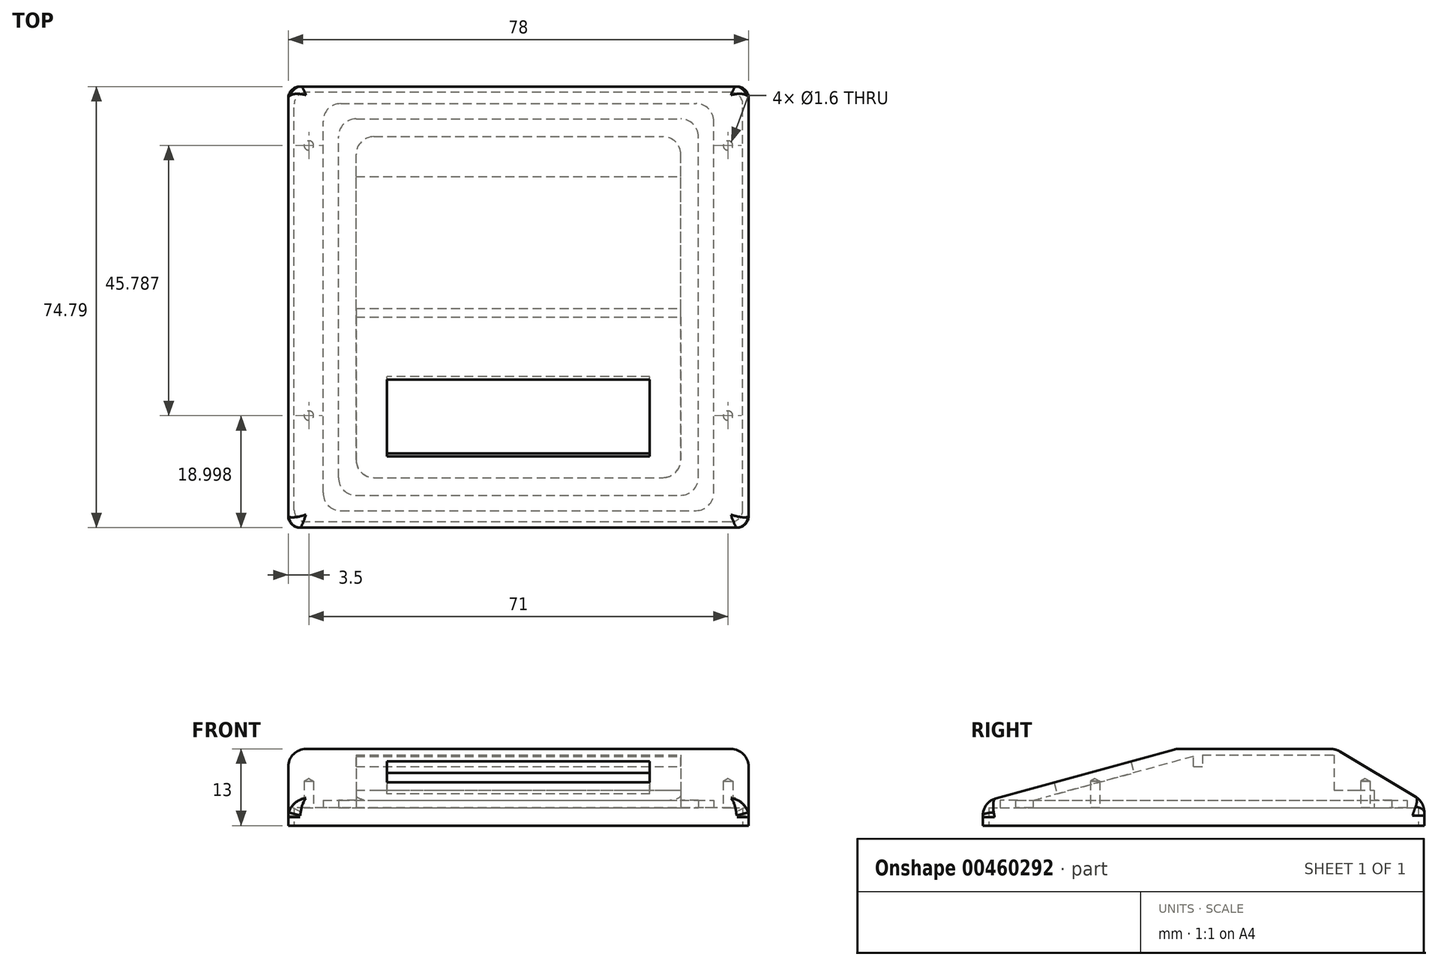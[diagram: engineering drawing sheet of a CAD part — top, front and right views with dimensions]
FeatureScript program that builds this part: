
annotation { "Feature Type Name" : "Feature", "Feature Type Description" : "" }
export const myFeature = defineFeature(function(context is Context, id is Id, definition is map)
    precondition{}
    {
        {
            var Q0;
            Q0=qCreatedBy(makeId("Right.planeOp"),FACE);
            var sketch = newSketch(context, id + "F0", { "sketchPlane" : qUnion([Q0])});
            skLineSegment(sketch, "E0", {"start": v(13.67, 15.98) * mm, "end": v(40.67, 15.98) * mm});
            skLineSegment(sketch, "E1", {"start": v(40.67, 15.98) * mm, "end": v(55.67, 6.98) * mm});
            skLineSegment(sketch, "E2", {"start": v(13.67, 15.98) * mm, "end": v(-19.12, 6.98) * mm});
            skLineSegment(sketch, "E3", {"start": v(-19.12, 6.98) * mm, "end": v(-19.12, 2.98) * mm});
            skLineSegment(sketch, "E4", {"start": v(-19.12, 2.98) * mm, "end": v(55.67, 2.98) * mm});
            skLineSegment(sketch, "E5", {"start": v(55.67, 6.98) * mm, "end": v(55.67, 2.98) * mm});
            skSolve(sketch);
        }
        {
            var Q0;
            Q0 = qSketchRegion(id + "F0", true);
            extrude(context, id + "F1", {"entities" : qUnion([Q0]), "depth" : 78 * mm, "offsetDistance" : 25 * mm});
        }
        {
            var Q0;
            Q0=makeQuery(id+"F1.opExtrude","CAP_FACE",FACE,{"disambiguationData":[OSD([sQuery(id+"F0.wireOp",EDGE,"E0"),sQuery(id+"F0.wireOp",EDGE,"E1"),sQuery(id+"F0.wireOp",EDGE,"E2"),sQuery(id+"F0.wireOp",EDGE,"E3"),sQuery(id+"F0.wireOp",EDGE,"E4"),sQuery(id+"F0.wireOp",EDGE,"E5")])],"isStart":false});
            cPlane(context, id + "F2", {"entities" : qUnion([Q0]), "cplaneType" : CPlaneType.OFFSET, "offset" : 11.5 * mm, "oppositeDirection" : true, "width" : 150 * mm, "height" : 150 * mm});
        }
        {
            var Q0;
            Q0=qCreatedBy(id+"F2.planeOp",FACE);
            var sketch = newSketch(context, id + "F3", { "sketchPlane" : qUnion([Q0])});
            skLineSegment(sketch, "E6.0", {"start": v(40.39, 14.98) * mm, "end": v(47.17, 10.92) * mm});
            skLineSegment(sketch, "E7.0", {"start": v(17.58, 14.98) * mm, "end": v(-10.62, 7.24) * mm});
            skLineSegment(sketch, "E8.0", {"start": v(-10.62, 2.98) * mm, "end": v(47.17, 2.98) * mm});
            skLineSegment(sketch, "E9", {"start": v(-10.62, 7.24) * mm, "end": v(-10.62, 2.98) * mm});
            skLineSegment(sketch, "E10", {"start": v(17.58, 14.98) * mm, "end": v(40.39, 14.98) * mm});
            skLineSegment(sketch, "E11", {"start": v(47.17, 10.92) * mm, "end": v(47.17, 2.98) * mm});
            skSolve(sketch);
        }
        {
            var Q0;
            Q0 = qSketchRegion(id + "F3", true);
            extrude(context, id + "F4", {"entities" : qUnion([Q0]), "operationType" : NewBodyOperationType.REMOVE, "oppositeDirection" : true, "depth" : 55 * mm, "offsetDistance" : 25 * mm});
        }
        {
            var Q0;
            Q0=makeQuery(id+"F4.boolean.opBoolean","COPY",FACE,{"derivedFrom":makeQuery(id+"F4.opExtrude","SWEPT_FACE",FACE,{"disambiguationData":[OSD([sQuery(id+"F3.wireOp",EDGE,"E7.0")])]})});
            var sketch = newSketch(context, id + "F5", { "sketchPlane" : qUnion([Q0])});
            skLineSegment(sketch, "E12.bottom", {"start": v(61.25, 4.08) * mm, "end": v(16.75, 4.08) * mm});
            skLineSegment(sketch, "E12.top", {"start": v(61.25, -9.42) * mm, "end": v(16.75, -9.42) * mm});
            skLineSegment(sketch, "E12.left", {"start": v(61.25, 4.08) * mm, "end": v(61.25, -9.42) * mm});
            skLineSegment(sketch, "E12.right", {"start": v(16.75, 4.08) * mm, "end": v(16.75, -9.42) * mm});
            skSolve(sketch);
        }
        {
            var Q0;
            Q0 = qSketchRegion(id + "F5", true);
            extrude(context, id + "F6", {"entities" : qUnion([Q0]), "operationType" : NewBodyOperationType.REMOVE, "endBound" : BoundingType.UP_TO_NEXT, "oppositeDirection" : true, "depth" : 25 * mm});
        }
        {
            var Q0;
            Q0=makeQuery(id+"F1.opExtrude","SWEPT_FACE",FACE,{"disambiguationData":[OSD([sQuery(id+"F0.wireOp",EDGE,"E4")])]});
            var sketch = newSketch(context, id + "F7", { "sketchPlane" : qUnion([Q0])});
            skLineSegment(sketch, "E13.0", {"start": v(77, 18.12) * mm, "end": v(77, -54.67) * mm});
            skLineSegment(sketch, "E13.1", {"start": v(77, 18.12) * mm, "end": v(1, 18.12) * mm});
            skLineSegment(sketch, "E13.2", {"start": v(1, 18.12) * mm, "end": v(1, -54.67) * mm});
            skLineSegment(sketch, "E13.3", {"start": v(77, -54.67) * mm, "end": v(1, -54.67) * mm});
            skLineSegment(sketch, "E14.0", {"start": v(66.5, 10.62) * mm, "end": v(66.5, -47.17) * mm});
            skLineSegment(sketch, "E14.1", {"start": v(11.5, 10.62) * mm, "end": v(66.5, 10.62) * mm});
            skLineSegment(sketch, "E14.2", {"start": v(11.5, 10.62) * mm, "end": v(11.5, -47.17) * mm});
            skLineSegment(sketch, "E14.3", {"start": v(11.5, -47.17) * mm, "end": v(66.5, -47.17) * mm});
            skPoint(sketch, "E15.visualSharp", {"position": v(77, 18.12) * mm});
            skPoint(sketch, "E16.visualSharp", {"position": v(1, 18.12) * mm});
            skPoint(sketch, "E17.visualSharp", {"position": v(77, -54.67) * mm});
            skPoint(sketch, "E18.visualSharp", {"position": v(1, -54.67) * mm});
            skSolve(sketch);
        }
        {
            var Q0;
            Q0 = qSketchRegion(id + "F7", true);
            extrude(context, id + "F8", {"entities" : qUnion([Q0]), "operationType" : NewBodyOperationType.REMOVE, "oppositeDirection" : true, "depth" : 3 * mm});
        }
        {
            var Q0;
            Q0=makeQuery(id+"F8.boolean.opBoolean","COPY",FACE,{"derivedFrom":makeQuery(id+"F8.opExtrude","CAP_FACE",FACE,{"disambiguationData":[OSD([sQuery(id+"F7.wireOp",EDGE,"E13.0"),sQuery(id+"F7.wireOp",EDGE,"E13.1"),sQuery(id+"F7.wireOp",EDGE,"E13.2"),sQuery(id+"F7.wireOp",EDGE,"E13.3"),sQuery(id+"F7.wireOp",EDGE,"E14.0"),sQuery(id+"F7.wireOp",EDGE,"E14.1"),sQuery(id+"F7.wireOp",EDGE,"E14.2"),sQuery(id+"F7.wireOp",EDGE,"E14.3"),sQuery(id+"F7.wireOp",EDGE,"E15.filletArc"),sQuery(id+"F7.wireOp",EDGE,"E16.filletArc"),sQuery(id+"F7.wireOp",EDGE,"E17.filletArc"),sQuery(id+"F7.wireOp",EDGE,"E18.filletArc")])],"isStart":false})});
            var sketch = newSketch(context, id + "F9", { "sketchPlane" : qUnion([Q0])});
            skLineSegment(sketch, "E19.0", {"start": v(69.5, 13.62) * mm, "end": v(69.5, -50.17) * mm});
            skLineSegment(sketch, "E19.1", {"start": v(8.5, 13.62) * mm, "end": v(69.5, 13.62) * mm});
            skLineSegment(sketch, "E19.2", {"start": v(8.5, 13.62) * mm, "end": v(8.5, -50.17) * mm});
            skLineSegment(sketch, "E19.3", {"start": v(8.5, -50.17) * mm, "end": v(69.5, -50.17) * mm});
            skLineSegment(sketch, "E20.0", {"start": v(72.1, 16.22) * mm, "end": v(72.1, -52.77) * mm});
            skLineSegment(sketch, "E20.1", {"start": v(5.9, 16.22) * mm, "end": v(72.1, 16.22) * mm});
            skLineSegment(sketch, "E20.2", {"start": v(5.9, 16.22) * mm, "end": v(5.9, -52.77) * mm});
            skLineSegment(sketch, "E20.3", {"start": v(5.9, -52.77) * mm, "end": v(72.1, -52.77) * mm});
            skSolve(sketch);
        }
        {
            var Q0;
            Q0 = qSketchRegion(id + "F9", true);
            extrude(context, id + "F10", {"entities" : qUnion([Q0]), "operationType" : NewBodyOperationType.REMOVE, "oppositeDirection" : true, "depth" : 1.3 * mm});
        }
        {
            var Q0;
            {var subQ0=sQuery(id+"F7.wireOp",EDGE,"E13.3");var subQ1=sQuery(id+"F7.wireOp",EDGE,"E13.2");var subQ2=sQuery(id+"F7.wireOp",EDGE,"E13.1");var subQ3=sQuery(id+"F7.wireOp",EDGE,"E13.0");Q0=makeQuery(id+"F10.boolean.opBoolean","SPLIT",FACE,{"disambiguationData":[TD([makeQuery(id+"F8.boolean.opBoolean","COPY",FACE,{"derivedFrom":makeQuery(id+"F8.opExtrude","SWEPT_FACE",FACE,{"disambiguationData":[OSD([subQ3])]})})])],"derivedFrom":makeQuery(id+"F8.boolean.opBoolean","COPY",FACE,{"derivedFrom":makeQuery(id+"F8.opExtrude","CAP_FACE",FACE,{"disambiguationData":[OSD([subQ3,subQ2,subQ1,subQ0,sQuery(id+"F7.wireOp",EDGE,"E14.0"),sQuery(id+"F7.wireOp",EDGE,"E14.1"),sQuery(id+"F7.wireOp",EDGE,"E14.2"),sQuery(id+"F7.wireOp",EDGE,"E14.3")])],"isStart":false})})});}
            var sketch = newSketch(context, id + "F11", { "sketchPlane" : qUnion([Q0])});
            skPoint(sketch, "E21", {"position": v(74.5, 0.12) * mm});
            skPoint(sketch, "E22", {"position": v(74.5, -45.67) * mm});
            skPoint(sketch, "E23", {"position": v(3.5, 0.12) * mm});
            skPoint(sketch, "E24", {"position": v(3.5, -45.67) * mm});
            skSolve(sketch);
        }
        {
            var Q0;
            Q0=sQuery(id+"F11.wireOp",VERTEX,"E24");
            var Q1;
            Q1=sQuery(id+"F11.wireOp",VERTEX,"E23");
            var Q2;
            Q2=sQuery(id+"F11.wireOp",VERTEX,"E21");
            var Q3;
            Q3=sQuery(id+"F11.wireOp",VERTEX,"E22");
            var Q4;
            Q4=makeQuery(id+"F1.opExtrude","SWEPT_BODY",BODY,{"disambiguationData":[OSD([sQuery(id+"F0.wireOp",EDGE,"E0"),sQuery(id+"F0.wireOp",EDGE,"E1"),sQuery(id+"F0.wireOp",EDGE,"E2"),sQuery(id+"F0.wireOp",EDGE,"E3"),sQuery(id+"F0.wireOp",EDGE,"E4"),sQuery(id+"F0.wireOp",EDGE,"E5")])]});
            hole(context, id + "F12", {"style" : HoleStyle.SIMPLE, "endStyle" : HoleEndStyle.BLIND, "holeDiameter" : 1.6 * mm, "holeDepth" : 4.5 * mm, "isTappedThrough" : true, "tappedDepth" : 12 * mm, "tapClearance" : 3, "startFromSketch" : true, "locations" : qUnion([Q0, Q1, Q2, Q3]), "scope" : qUnion([Q4])});
        }
        {
            var Q0;
            Q0=makeQuery(id+"F8.boolean.opBoolean","COPY",EDGE,{"derivedFrom":makeQuery(id+"F8.opExtrude","SWEPT_EDGE",EDGE,{"disambiguationData":[OSD([sQuery(id+"F7.wireOp",EDGE,"E13.0"),sQuery(id+"F7.wireOp",EDGE,"E13.3")])]})});
            var Q1;
            Q1=makeQuery(id+"F8.boolean.opBoolean","COPY",EDGE,{"derivedFrom":makeQuery(id+"F8.opExtrude","SWEPT_EDGE",EDGE,{"disambiguationData":[OSD([sQuery(id+"F7.wireOp",EDGE,"E13.0"),sQuery(id+"F7.wireOp",EDGE,"E13.1")])]})});
            var Q2;
            Q2=makeQuery(id+"F8.boolean.opBoolean","COPY",EDGE,{"derivedFrom":makeQuery(id+"F8.opExtrude","SWEPT_EDGE",EDGE,{"disambiguationData":[OSD([sQuery(id+"F7.wireOp",EDGE,"E13.2"),sQuery(id+"F7.wireOp",EDGE,"E13.3")])]})});
            var Q3;
            Q3=makeQuery(id+"F8.boolean.opBoolean","COPY",EDGE,{"derivedFrom":makeQuery(id+"F8.opExtrude","SWEPT_EDGE",EDGE,{"disambiguationData":[OSD([sQuery(id+"F7.wireOp",EDGE,"E13.1"),sQuery(id+"F7.wireOp",EDGE,"E13.2")])]})});
            var Q4;
            Q4=makeQuery(id+"F1.opExtrude","CAP_EDGE",EDGE,{"disambiguationData":[OSD([sQuery(id+"F0.wireOp",EDGE,"E3")])],"isStart":true});
            var Q5;
            Q5=makeQuery(id+"F1.opExtrude","CAP_EDGE",EDGE,{"disambiguationData":[OSD([sQuery(id+"F0.wireOp",EDGE,"E3")])],"isStart":false});
            var Q6;
            Q6=makeQuery(id+"F1.opExtrude","CAP_EDGE",EDGE,{"disambiguationData":[OSD([sQuery(id+"F0.wireOp",EDGE,"E5")])],"isStart":false});
            var Q7;
            Q7=makeQuery(id+"F1.opExtrude","CAP_EDGE",EDGE,{"disambiguationData":[OSD([sQuery(id+"F0.wireOp",EDGE,"E5")])],"isStart":true});
            fillet(context, id + "F13", {"entities" : qUnion([Q0, Q1, Q2, Q3, Q4, Q5, Q6, Q7]), "radius" : 2 * mm, "tangentPropagation" : true, "allowEdgeOverflow" : false});
        }
        {
            var Q0;
            Q0=makeQuery(id+"F10.boolean.opBoolean","COPY",EDGE,{"derivedFrom":makeQuery(id+"F10.opExtrude","SWEPT_EDGE",EDGE,{"disambiguationData":[OSD([sQuery(id+"F9.wireOp",EDGE,"E20.0"),sQuery(id+"F9.wireOp",EDGE,"E20.1")])]})});
            var Q1;
            Q1=makeQuery(id+"F10.boolean.opBoolean","COPY",EDGE,{"derivedFrom":makeQuery(id+"F10.opExtrude","SWEPT_EDGE",EDGE,{"disambiguationData":[OSD([sQuery(id+"F9.wireOp",EDGE,"E20.0"),sQuery(id+"F9.wireOp",EDGE,"E20.3")])]})});
            var Q2;
            Q2=makeQuery(id+"F10.boolean.opBoolean","COPY",EDGE,{"derivedFrom":makeQuery(id+"F10.opExtrude","SWEPT_EDGE",EDGE,{"disambiguationData":[OSD([sQuery(id+"F9.wireOp",EDGE,"E20.1"),sQuery(id+"F9.wireOp",EDGE,"E20.2")])]})});
            var Q3;
            Q3=makeQuery(id+"F10.boolean.opBoolean","COPY",EDGE,{"derivedFrom":makeQuery(id+"F10.opExtrude","SWEPT_EDGE",EDGE,{"disambiguationData":[OSD([sQuery(id+"F9.wireOp",EDGE,"E20.2"),sQuery(id+"F9.wireOp",EDGE,"E20.3")])]})});
            var Q4;
            Q4=makeQuery(id+"F10.boolean.opBoolean","COPY",EDGE,{"derivedFrom":makeQuery(id+"F10.opExtrude","SWEPT_EDGE",EDGE,{"disambiguationData":[OSD([sQuery(id+"F9.wireOp",EDGE,"E19.1"),sQuery(id+"F9.wireOp",EDGE,"E19.2")])]})});
            var Q5;
            Q5=makeQuery(id+"F10.boolean.opBoolean","COPY",EDGE,{"derivedFrom":makeQuery(id+"F10.opExtrude","SWEPT_EDGE",EDGE,{"disambiguationData":[OSD([sQuery(id+"F9.wireOp",EDGE,"E19.0"),sQuery(id+"F9.wireOp",EDGE,"E19.1")])]})});
            var Q6;
            Q6=makeQuery(id+"F10.boolean.opBoolean","COPY",EDGE,{"derivedFrom":makeQuery(id+"F10.opExtrude","SWEPT_EDGE",EDGE,{"disambiguationData":[OSD([sQuery(id+"F9.wireOp",EDGE,"E19.0"),sQuery(id+"F9.wireOp",EDGE,"E19.3")])]})});
            var Q7;
            Q7=makeQuery(id+"F10.boolean.opBoolean","COPY",EDGE,{"derivedFrom":makeQuery(id+"F10.opExtrude","SWEPT_EDGE",EDGE,{"disambiguationData":[OSD([sQuery(id+"F9.wireOp",EDGE,"E19.2"),sQuery(id+"F9.wireOp",EDGE,"E19.3")])]})});
            var Q8;
            Q8=makeQuery(id+"F4.boolean.opBoolean","COPY",EDGE,{"derivedFrom":makeQuery(id+"F4.opExtrude","CAP_EDGE",EDGE,{"disambiguationData":[OSD([sQuery(id+"F3.wireOp",EDGE,"E9")])],"isStart":false})});
            var Q9;
            Q9=makeQuery(id+"F4.boolean.opBoolean","COPY",EDGE,{"derivedFrom":makeQuery(id+"F4.opExtrude","CAP_EDGE",EDGE,{"disambiguationData":[OSD([sQuery(id+"F3.wireOp",EDGE,"E9")])],"isStart":true})});
            var Q10;
            Q10=makeQuery(id+"F4.boolean.opBoolean","COPY",EDGE,{"derivedFrom":makeQuery(id+"F4.opExtrude","CAP_EDGE",EDGE,{"disambiguationData":[OSD([sQuery(id+"F3.wireOp",EDGE,"E11")])],"isStart":true})});
            var Q11;
            Q11=makeQuery(id+"F4.boolean.opBoolean","COPY",EDGE,{"derivedFrom":makeQuery(id+"F4.opExtrude","CAP_EDGE",EDGE,{"disambiguationData":[OSD([sQuery(id+"F3.wireOp",EDGE,"E11")])],"isStart":false})});
            fillet(context, id + "F14", {"entities" : qUnion([Q0, Q1, Q2, Q3, Q4, Q5, Q6, Q7, Q8, Q9, Q10, Q11]), "radius" : 3 * mm, "tangentPropagation" : true, "allowEdgeOverflow" : false});
        }
        {
            var Q0;
            Q0=makeQuery(id+"F1.opExtrude","CAP_EDGE",EDGE,{"disambiguationData":[OSD([sQuery(id+"F0.wireOp",EDGE,"E2")])],"isStart":true});
            var Q1;
            Q1=makeQuery(id+"F1.opExtrude","CAP_EDGE",EDGE,{"disambiguationData":[OSD([sQuery(id+"F0.wireOp",EDGE,"E0")])],"isStart":true});
            var Q2;
            Q2=makeQuery(id+"F1.opExtrude","CAP_EDGE",EDGE,{"disambiguationData":[OSD([sQuery(id+"F0.wireOp",EDGE,"E1")])],"isStart":true});
            var Q3;
            Q3=makeQuery(id+"F1.opExtrude","CAP_EDGE",EDGE,{"disambiguationData":[OSD([sQuery(id+"F0.wireOp",EDGE,"E2")])],"isStart":false});
            var Q4;
            Q4=makeQuery(id+"F1.opExtrude","SWEPT_EDGE",EDGE,{"disambiguationData":[OSD([sQuery(id+"F0.wireOp",EDGE,"E2"),sQuery(id+"F0.wireOp",EDGE,"E3")])]});
            var Q5;
            Q5=makeQuery(id+"F1.opExtrude","SWEPT_EDGE",EDGE,{"disambiguationData":[OSD([sQuery(id+"F0.wireOp",EDGE,"E0"),sQuery(id+"F0.wireOp",EDGE,"E2")])]});
            var Q6;
            Q6=makeQuery(id+"F1.opExtrude","CAP_EDGE",EDGE,{"disambiguationData":[OSD([sQuery(id+"F0.wireOp",EDGE,"E0")])],"isStart":false});
            var Q7;
            Q7=makeQuery(id+"F1.opExtrude","CAP_EDGE",EDGE,{"disambiguationData":[OSD([sQuery(id+"F0.wireOp",EDGE,"E1")])],"isStart":false});
            var Q8;
            Q8=makeQuery(id+"F1.opExtrude","SWEPT_EDGE",EDGE,{"disambiguationData":[OSD([sQuery(id+"F0.wireOp",EDGE,"E0"),sQuery(id+"F0.wireOp",EDGE,"E1")])]});
            var Q9;
            Q9=makeQuery(id+"F13.opFillet","BLEND_EDGE",EDGE,{"blendedFrom":[makeQuery(id+"F1.opExtrude","CAP_EDGE",EDGE,{"disambiguationData":[OSD([sQuery(id+"F0.wireOp",EDGE,"E5")])],"isStart":false}),makeQuery(id+"F1.opExtrude","SWEPT_FACE",FACE,{"disambiguationData":[OSD([sQuery(id+"F0.wireOp",EDGE,"E1")])]})],"blendedInto":[makeQuery(id+"F1.opExtrude","SWEPT_FACE",FACE,{"disambiguationData":[OSD([sQuery(id+"F0.wireOp",EDGE,"E1")])]})]});
            var Q10;
            Q10=makeQuery(id+"F1.opExtrude","SWEPT_EDGE",EDGE,{"disambiguationData":[OSD([sQuery(id+"F0.wireOp",EDGE,"E1"),sQuery(id+"F0.wireOp",EDGE,"E5")])]});
            var Q11;
            Q11=makeQuery(id+"F13.opFillet","BLEND_EDGE",EDGE,{"blendedFrom":[makeQuery(id+"F1.opExtrude","CAP_EDGE",EDGE,{"disambiguationData":[OSD([sQuery(id+"F0.wireOp",EDGE,"E5")])],"isStart":true}),makeQuery(id+"F1.opExtrude","SWEPT_FACE",FACE,{"disambiguationData":[OSD([sQuery(id+"F0.wireOp",EDGE,"E1")])]})],"blendedInto":[makeQuery(id+"F1.opExtrude","SWEPT_FACE",FACE,{"disambiguationData":[OSD([sQuery(id+"F0.wireOp",EDGE,"E1")])]})]});
            var Q12;
            Q12=makeQuery(id+"F13.opFillet","BLEND_EDGE",EDGE,{"blendedFrom":[makeQuery(id+"F1.opExtrude","CAP_EDGE",EDGE,{"disambiguationData":[OSD([sQuery(id+"F0.wireOp",EDGE,"E3")])],"isStart":false}),makeQuery(id+"F1.opExtrude","SWEPT_FACE",FACE,{"disambiguationData":[OSD([sQuery(id+"F0.wireOp",EDGE,"E2")])]})],"blendedInto":[makeQuery(id+"F1.opExtrude","SWEPT_FACE",FACE,{"disambiguationData":[OSD([sQuery(id+"F0.wireOp",EDGE,"E2")])]})]});
            var Q13;
            Q13=makeQuery(id+"F13.opFillet","BLEND_EDGE",EDGE,{"blendedFrom":[makeQuery(id+"F1.opExtrude","CAP_EDGE",EDGE,{"disambiguationData":[OSD([sQuery(id+"F0.wireOp",EDGE,"E3")])],"isStart":true}),makeQuery(id+"F1.opExtrude","SWEPT_FACE",FACE,{"disambiguationData":[OSD([sQuery(id+"F0.wireOp",EDGE,"E2")])]})],"blendedInto":[makeQuery(id+"F1.opExtrude","SWEPT_FACE",FACE,{"disambiguationData":[OSD([sQuery(id+"F0.wireOp",EDGE,"E2")])]})]});
            fillet(context, id + "F15", {"entities" : qUnion([Q0, Q1, Q2, Q3, Q4, Q5, Q6, Q7, Q8, Q9, Q10, Q11, Q12, Q13]), "radius" : 3 * mm, "tangentPropagation" : true, "allowEdgeOverflow" : false});
        }
        {
            var Q0;
            Q0=makeQuery(id+"F4.boolean.opBoolean","COPY",FACE,{"derivedFrom":makeQuery(id+"F4.opExtrude","CAP_FACE",FACE,{"disambiguationData":[OSD([sQuery(id+"F3.wireOp",EDGE,"E6.0"),sQuery(id+"F3.wireOp",EDGE,"E7.0"),sQuery(id+"F3.wireOp",EDGE,"E8.0"),sQuery(id+"F3.wireOp",EDGE,"E9"),sQuery(id+"F3.wireOp",EDGE,"E10"),sQuery(id+"F3.wireOp",EDGE,"E11")])],"isStart":true})});
            var sketch = newSketch(context, id + "F16", { "sketchPlane" : qUnion([Q0])});
            skLineSegment(sketch, "E25", {"start": v(-17.58, 14.98) * mm, "end": v(-18.08, 14.98) * mm});
            skLineSegment(sketch, "E26", {"start": v(-16.58, 12.98) * mm, "end": v(-18.08, 12.98) * mm});
            skLineSegment(sketch, "E27", {"start": v(-18.08, 14.98) * mm, "end": v(-18.08, 12.98) * mm});
            skLineSegment(sketch, "E28", {"start": v(-16.58, 12.98) * mm, "end": v(-16.58, 14.7) * mm});
            skLineSegment(sketch, "E29", {"start": v(-17.58, 14.98) * mm, "end": v(-16.58, 14.7) * mm});
            skSolve(sketch);
        }
        {
            var Q0;
            Q0=makeQuery(id+"F16.imprint","IMPRINT",FACE,{"disambiguationData":[TD([[makeQuery(id+"F16.imprint","IMPRINT",EDGE,{"derivedFrom":sQuery(id+"F16.wireOp",EDGE,"E25")}),1.0]])]});
            extrude(context, id + "F17", {"entities" : qUnion([Q0]), "operationType" : NewBodyOperationType.ADD, "endBound" : BoundingType.UP_TO_NEXT, "depth" : 25 * mm});
        }
        {
            var Q0;
            {var subQ0=sQuery(id+"F3.wireOp",EDGE,"E9");Q0=makeQuery(id+"F10.boolean.opBoolean","SPLIT",FACE,{"disambiguationData":[TD([makeQuery(id+"F4.boolean.opBoolean","COPY",FACE,{"derivedFrom":makeQuery(id+"F4.opExtrude","SWEPT_FACE",FACE,{"disambiguationData":[OSD([subQ0])]})})])],"derivedFrom":makeQuery(id+"F8.boolean.opBoolean","COPY",FACE,{"derivedFrom":makeQuery(id+"F8.opExtrude","CAP_FACE",FACE,{"disambiguationData":[OSD([sQuery(id+"F7.wireOp",EDGE,"E13.0"),sQuery(id+"F7.wireOp",EDGE,"E13.1"),sQuery(id+"F7.wireOp",EDGE,"E13.2"),sQuery(id+"F7.wireOp",EDGE,"E13.3"),sQuery(id+"F7.wireOp",EDGE,"E14.0"),sQuery(id+"F7.wireOp",EDGE,"E14.1"),sQuery(id+"F7.wireOp",EDGE,"E14.2"),sQuery(id+"F7.wireOp",EDGE,"E14.3")])],"isStart":false})})});}
            cPlane(context, id + "F18", {"entities" : qUnion([Q0]), "cplaneType" : CPlaneType.OFFSET, "offset" : 3 * mm, "oppositeDirection" : true, "width" : 150 * mm, "height" : 150 * mm});
        }
        {
            var Q0;
            Q0=qCreatedBy(id+"F18.planeOp",FACE);
            var sketch = newSketch(context, id + "F19", { "sketchPlane" : qUnion([Q0])});
            skLineSegment(sketch, "E30.1", {"start": v(14.5, -47.17) * mm, "end": v(63.5, -47.17) * mm});
            skArc(sketch, "E30.2", {"start": v(66.5, -44.17) * mm, "mid": v(65.62, -46.29) * mm, "end": v(63.5, -47.17) * mm});
            skLineSegment(sketch, "E31", {"start": v(66.5, -40.39) * mm, "end": v(66.5, -44.17) * mm});
            skLineSegment(sketch, "E32", {"start": v(11.5, -40.39) * mm, "end": v(66.5, -40.39) * mm});
            skArc(sketch, "E33", {"start": v(11.5, -44.17) * mm, "mid": v(12.38, -46.29) * mm, "end": v(14.5, -47.17) * mm});
            skLineSegment(sketch, "E34", {"start": v(11.5, -40.39) * mm, "end": v(11.5, -44.17) * mm});
            skSolve(sketch);
        }
        {
            var Q0;
            Q0 = qSketchRegion(id + "F19", true);
            extrude(context, id + "F20", {"entities" : qUnion([Q0]), "operationType" : NewBodyOperationType.ADD, "endBound" : BoundingType.UP_TO_NEXT, "oppositeDirection" : true, "depth" : 25 * mm, "offsetDistance" : 25 * mm});
        }
    });
